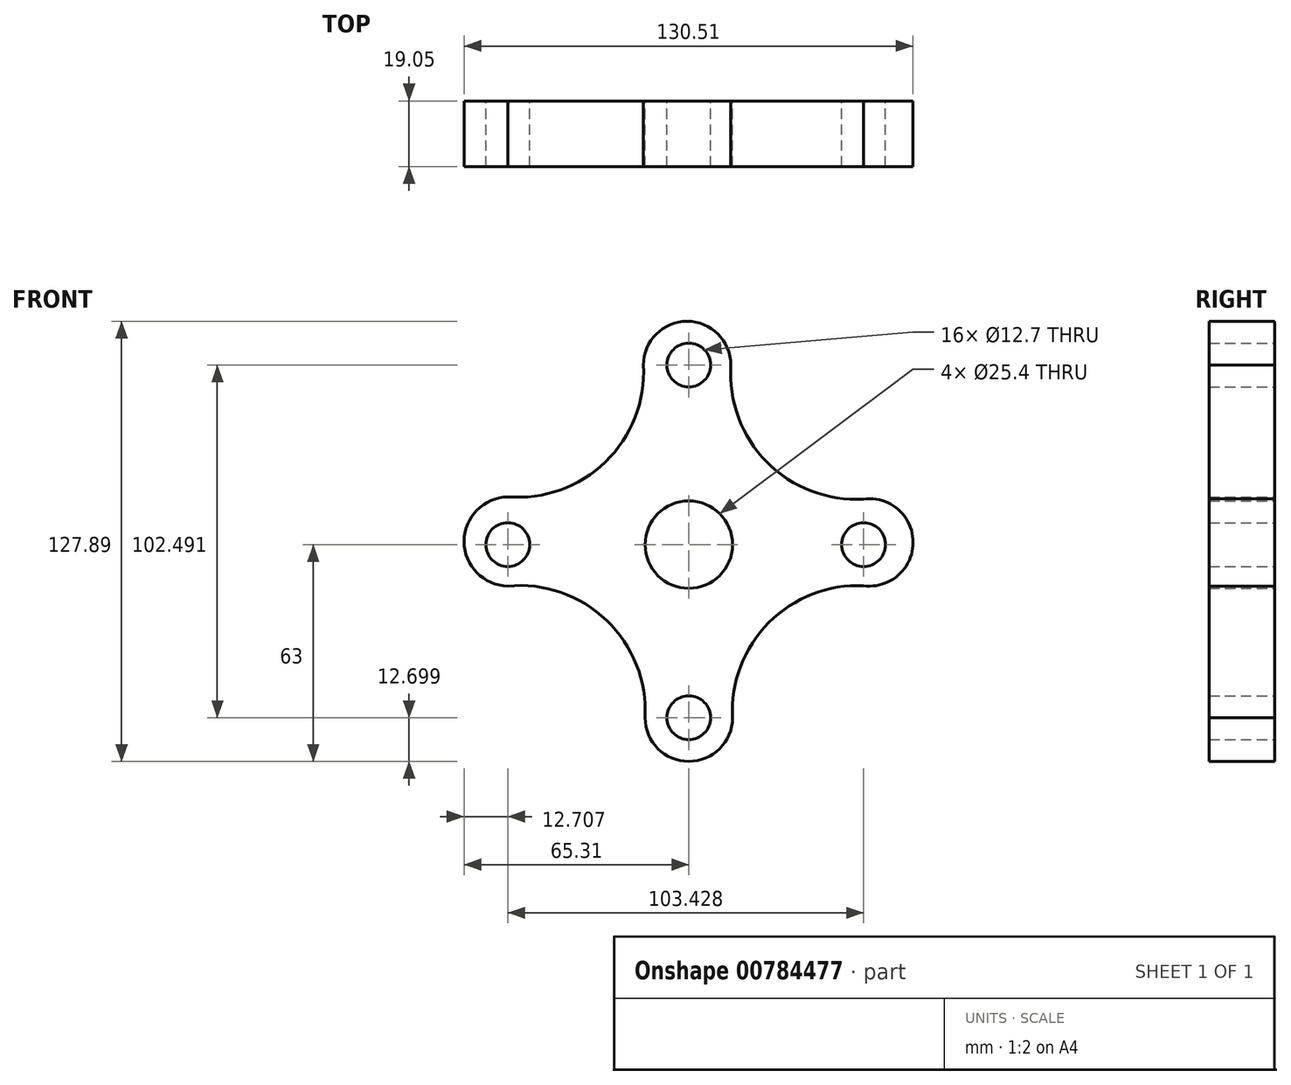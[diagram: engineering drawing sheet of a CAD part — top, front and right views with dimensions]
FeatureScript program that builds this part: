
annotation { "Feature Type Name" : "Feature", "Feature Type Description" : "" }
export const myFeature = defineFeature(function(context is Context, id is Id, definition is map)
    precondition{}
    {
        {
            var Q0;
            Q0=qCreatedBy(makeId("Front.planeOp"),FACE);
            var sketch = newSketch(context, id + "F0", { "sketchPlane" : qUnion([Q0])});
            skCircle(sketch, "E0", {"center": v(0, 0) * mm, "radius": 12.7 * mm});
            skCircle(sketch, "E1", {"center": v(0, 52.2) * mm, "radius": 6.35 * mm});
            skCircle(sketch, "E2", {"center": v(0, -50.3) * mm, "radius": 6.35 * mm});
            skCircle(sketch, "E3", {"center": v(50.83, 0) * mm, "radius": 6.35 * mm});
            skCircle(sketch, "E4", {"center": v(-52.6, 0) * mm, "radius": 6.35 * mm});
            skLineSegment(sketch, "E5", {"start": v(-52.6, 0) * mm, "end": v(-52.6, 13.87) * mm});
            skLineSegment(sketch, "E6", {"start": v(0, 52.2) * mm, "end": v(-13.17, 52.2) * mm});
            skLineSegment(sketch, "E7", {"start": v(0, 52.2) * mm, "end": v(12.23, 52.2) * mm});
            skLineSegment(sketch, "E8", {"start": v(0, 52.2) * mm, "end": v(0, 64.88) * mm});
            skLineSegment(sketch, "E9", {"start": v(50.83, 0) * mm, "end": v(50.83, 13.23) * mm});
            skLineSegment(sketch, "E10", {"start": v(50.83, 0) * mm, "end": v(50.83, -11.94) * mm});
            skLineSegment(sketch, "E11", {"start": v(50.83, 0) * mm, "end": v(65.19, 0) * mm});
            skArc(sketch, "E12", {"start": v(50.83, -11.94) * mm, "mid": v(65.2, 0.65) * mm, "end": v(50.83, 13.23) * mm});
            skArc(sketch, "E13", {"start": v(12.23, 52.2) * mm, "mid": v(-0.47, 64.9) * mm, "end": v(-13.17, 52.2) * mm});
            skLineSegment(sketch, "E14", {"start": v(-52.6, 0) * mm, "end": v(-52.6, -12.03) * mm});
            skLineSegment(sketch, "E15", {"start": v(-52.6, 0) * mm, "end": v(-65.27, 0) * mm});
            skArc(sketch, "E16", {"start": v(-52.6, 13.87) * mm, "mid": v(-65.3, 0.92) * mm, "end": v(-52.6, -12.03) * mm});
            skLineSegment(sketch, "E17", {"start": v(0, -50.3) * mm, "end": v(12.7, -50.3) * mm});
            skLineSegment(sketch, "E18", {"start": v(0, -50.3) * mm, "end": v(-12.7, -50.3) * mm});
            skLineSegment(sketch, "E19", {"start": v(0, -50.3) * mm, "end": v(0, -63) * mm});
            skArc(sketch, "E20", {"start": v(-12.7, -50.3) * mm, "mid": v(0, -63) * mm, "end": v(12.7, -50.3) * mm});
            skArc(sketch, "E21", {"start": v(-52.6, 13.87) * mm, "mid": v(-24.19, 24.08) * mm, "end": v(-13.17, 52.2) * mm});
            skArc(sketch, "E22", {"start": v(12.23, 52.2) * mm, "mid": v(22.72, 23.99) * mm, "end": v(50.83, 13.23) * mm});
            skArc(sketch, "E23", {"start": v(50.83, -11.94) * mm, "mid": v(23.27, -22.68) * mm, "end": v(12.7, -50.3) * mm});
            skArc(sketch, "E24", {"start": v(-12.7, -50.3) * mm, "mid": v(-23.89, -22.03) * mm, "end": v(-52.6, -12.03) * mm});
            skSolve(sketch);
        }
        {
            var Q0;
            Q0 = qSketchRegion(id + "F0", true);
            extrude(context, id + "F1", {"entities" : qUnion([Q0]), "depth" : 19.05 * mm, "offsetDistance" : 25.4 * mm});
        }
    });
